# Revit family: Gira_126967
name_source: partatom
category: Elektroinstallationen
revit_build: Autodesk Revit 2017 (Build: 20160225_1515(x64)
units: mm (PartAtom-declared; Revit-internal decimal feet)

## family parameters
Basisbauteil = Fläche
Beim Laden mit Abzugskörper schneiden = Nein
Bemaßung runder Anschluss = Durchmesser verwenden
Beschriftungsausrichtung beibehalten = Nein
Gemeinsam genutzt = Nein
Raumberechnungspunkt = Nein
Teiletyp = Normal

## types (1)
- Gira_126967
    Anzahl der Ruftasten = 1
    BIM = https://media.stage.bim.site AP 1fach_Türko.rfa
    Beschreibung = Türstation Video AP 1fach  Anthrazit Merkmale: - Komplett vormontierte Türstation AP für die senkrechte Aufputz-Montage. Dadurch schnelle und saubere Montage möglich. - Im Design des Schalterprogramms Gira TX_44. - Verwindungssteifes Aufputz-Gehäuse durch Aluminiumprofil. - Abdeckrahmen aus bruchsicherem Thermoplast mit hoher UV-Stabilität sowie einer kratzfesten, pflegeleichten Oberfläche. - Diebstahlschutz mittels Torx-Schrauben. - Signalübertragung und Versorgung der Audio- und Videokomponenten über verpolungssicheren und kurzschlussfesten 2-Draht-Bus. - Einmann-Inbetriebnahme durch einfache Inbetriebnahme-Prozedur. - Wetterfester Lautsprecher. - Hochwertiges Elektretmikrofon. - Freisprechfunktion (sprachgesteuertes Gegensprechen mit Echo- und Hintergrund-geräuschunterdrückung). - Akustisches Quittiersignal bei Ruftastenbetätigung. - Sprechlautstärke einstellbar. - Weiße Ruftastenausleuchtung in LED-Technologie. Durch die wartungsfreie und stromsparende LED-Technologie wird eine gleichmäßige, gut sichtbare Ruftastenausleuchtung erreicht. - Spritzwasserdichte Ruftastenabdeckung aus schlagfestem Kunststoff. - Namensschild des Ruftasters ohne Werkzeug und ohne Rahmendemontage austauschbar.  - Professionelle Beschriftung über den Gira Beschriftungsservice www.beschriftung.gira.de oder die Gira Beschriftungssoftware. - Türstation mit Farbkamera, Türlautsprecher und Ruftaster. - Automatische Tag- bzw. Nachtumschaltung: Die Kamera schaltet ab einer definierten Umgebungshelligkeit von Tagbetrieb (Farbdarstellung) auf Nachtbetrieb (Schwarz-Weiß-Darstellung) und umgekehrt. Aufgrund der hohen Lichtempfindlichkeit im Nachtbetrieb werden gute Darstellungsergebnisse auch bei schlechten Lichtverhältnissen erreicht. - Leuchtdioden sorgen im Nachtbetrieb für eine gleichmäßige Gesichtsfeldausleuchtung im Nahbereich. - Kamera horizontal und vertikal um 20 manuell schwenkbar. In Kombination mit dem Weitwinkelobjektiv ergibt sich daraus ein sehr großer Sichtwinkel. - Automatische Gegenlichtkompensation. - Automatischer Weißabgleich. - Automatische Verstärkungsregelung (AGC). - Integrierte Kameraheizung mit Temperaturerfassung. - Spritzwasserdichte Abdeckung. - Kameraabdeckung aus schlagfestem Kunststoff, bei Beschädigung, z. B. durch Vandalismus, leicht austauschbar.
    Datenblatt = https://katalog.gira.de
    Farbe = anthrazit
    GTIN = 4010337269670
    HAN = 126967
    Hersteller = Gira
    Installationstechnik = Bus-System
    Mit Abdeckung = Ja
    Mit Infoschild = Ja
    Mit Kamera = Ja
    Modulare Bauweise = Ja
    Montageart = Aufputz
    Produktseite = http://katalog.gira.de
    Schutz gegen Vandalismus = Ja
    Typname = Türstation Video AP 1f Türko Anthrazit
    URL = https://www.gira.de
    Vorgabe-Ansicht = 1219 mm

## geometry (parser evidence)
native form markers: Sweep x2
no freeform markers — native parametric forms only
